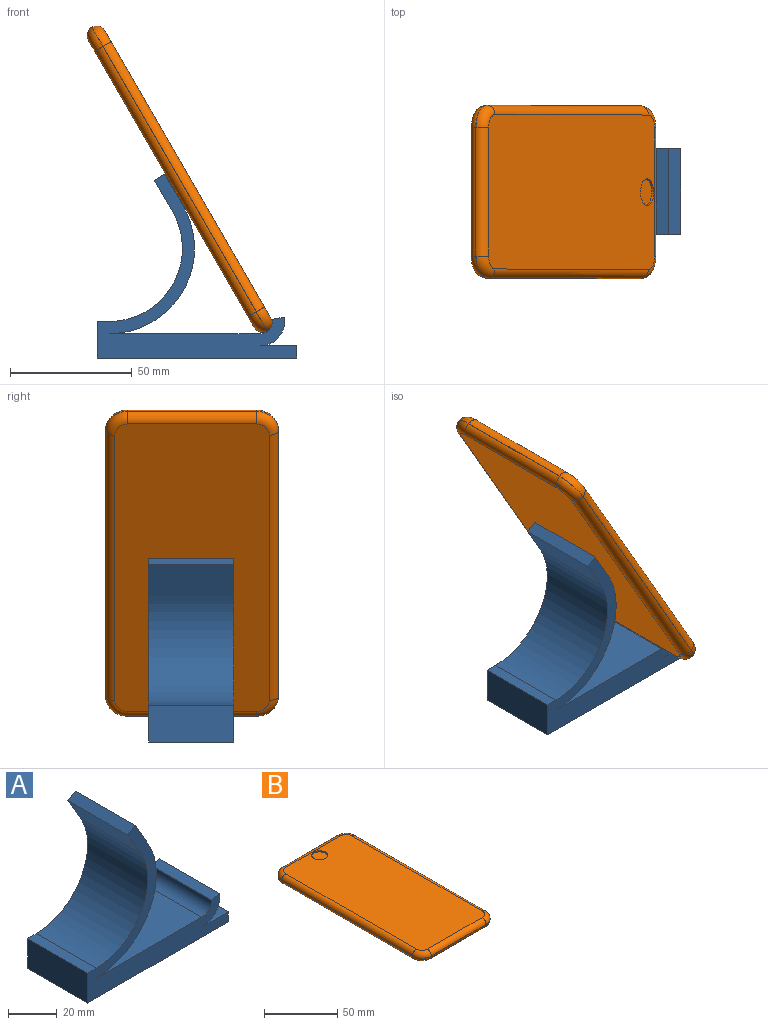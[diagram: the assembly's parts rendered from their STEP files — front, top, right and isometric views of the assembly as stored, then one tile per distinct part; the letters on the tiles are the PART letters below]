
ASSEMBLY  parts=2 mates=1
PART A: 23 faces, bbox 82x35x75.5 mm
  f0: plane 82x35mm, normal (0,0,-1), area 666mm2, adj f1,f2,f4,f16,f17,f18,f21,f22
  f1: plane 76x8mm, normal (0,1,0), area 528mm2, adj f0,f3,f18,f19,f20,f22
  f2: plane 76x8mm, normal (0,-1,0), area 528mm2, adj f0,f3,f18,f19,f20,f22
  f3: plane 60x29mm, normal (0,0,-1), area 1740mm2, adj f1,f2,f20,f22
  f4: plane 35x5mm, normal (1,0,0), area 175mm2, adj f0,f5,f16,f17
  f5: plane 35x15mm, normal (0,0,1), area 525mm2, adj f4,f6,f16,f17
  f6: cylinder r=10mm len=35mm, axis (0,1,0), area 611mm2, adj f5,f7,f16,f17
  f7: plane 35x4.92mm, normal (-0.17,0,0.98), area 175mm2, adj f6,f8,f16,f17
  f8: cylinder r=5mm len=35mm, axis (0,1,0), area 322.9mm2, adj f7,f9,f16,f17
  f9: plane 61.5x35mm, normal (0,0,1), area 2152.6mm2, adj f8,f10,f16,f17
  f10: cylinder r=35mm len=52.5mm, axis (0,1,0), area 2565.6mm2, adj f9,f11,f16,f17
  f11: plane 35x12.99mm, normal (0.87,0,0.5), area 525mm2, adj f10,f12,f16,f17
  f12: plane 35x4.33mm, normal (-0.5,0,0.87), area 175mm2, adj f11,f13,f16,f17
  f13: plane 35x12.99mm, normal (-0.87,0,-0.5), area 525mm2, adj f12,f14,f16,f17
  f14: cylinder r=30mm len=45mm, axis (0,1,0), area 2199.1mm2, adj f13,f15,f16,f17
  f15: plane 35x5mm, normal (0,0,1), area 175mm2, adj f14,f16,f17,f21
  f16: plane 82x75.49mm, normal (0,-1,0), area 1251.6mm2, adj f0,f4,f5,f6,f7,f8,f9,f10
  f17: plane 82x75.49mm, normal (0,1,0), area 1251.6mm2, adj f0,f4,f5,f6,f7,f8,f9,f10
  f18: plane 29x3mm, normal (-1,0,0), area 87mm2, adj f0,f1,f2,f19
  f19: plane 29x16mm, normal (0,0,-1), area 464mm2, adj f1,f2,f18,f20
  f20: plane 29x5mm, normal (-1,0,0), area 145mm2, adj f1,f2,f3,f19
  f21: plane 35x15mm, normal (-1,0,0), area 525mm2, adj f0,f15,f16,f17
  f22: plane 29x8mm, normal (1,0,0), area 232mm2, adj f0,f1,f2,f3
PART B: 28 faces, bbox 72.5x145.5x7.7 mm
  f0: plane 125.8x0.09mm, normal (1,0,0), area 11.3mm2, adj f7,f9,f11,f20
  f1: plane 136.4x63.4mm, normal (0,0,1), area 8530.3mm2, adj f10,f11,f12,f13,f14,f15,f16,f17
  f2: plane 125.8x0.09mm, normal (-1,0,0), area 11.3mm2, adj f6,f8,f16,f23
  f3: plane 136.4x63.4mm, normal (0,0,-1), area 8623.6mm2, adj f18,f19,f20,f21,f22,f23,f24,f25
  f4: plane 52.8x0.09mm, normal (0,-1,0), area 4.8mm2, adj f8,f9,f12,f19
  f5: plane 52.8x0.09mm, normal (0,1,0), area 4.8mm2, adj f6,f7,f15,f24
  f6: cylinder r=9.1mm len=9.1mm, axis (0,0,-1), area 1.3mm2, adj f2,f5,f17,f25
  f7: cylinder r=9.1mm len=9.1mm, axis (0,0,1), area 1.3mm2, adj f0,f5,f13,f22
  f8: cylinder r=9.1mm len=9.1mm, axis (0,0,1), area 1.3mm2, adj f2,f4,f14,f21
  f9: cylinder r=9.1mm len=9.1mm, axis (0,0,-1), area 1.3mm2, adj f0,f4,f10,f18
  f10: torus R=5.3mm, axis (0,0,-1), area 72.4mm2, adj f1,f9,f11,f12
  f11: cylinder r=3.8mm len=125.8mm, axis (0,-1,0), area 750.9mm2, adj f0,f1,f10,f13
  f12: cylinder r=3.8mm len=52.8mm, axis (1,0,0), area 315.2mm2, adj f1,f4,f10,f14
  f13: torus R=5.3mm, axis (0,0,-1), area 72.4mm2, adj f1,f7,f11,f15
  f14: torus R=5.3mm, axis (0,0,-1), area 72.4mm2, adj f1,f8,f12,f16
  f15: cylinder r=3.8mm len=52.8mm, axis (-1,0,0), area 315.2mm2, adj f1,f5,f13,f17
  f16: cylinder r=3.8mm len=125.8mm, axis (0,1,0), area 750.9mm2, adj f1,f2,f14,f17
  f17: torus R=5.3mm, axis (0,0,-1), area 72.4mm2, adj f1,f6,f15,f16
  f18: torus R=5.3mm, axis (0,0,-1), area 72.4mm2, adj f3,f9,f19,f20
  f19: cylinder r=3.8mm len=52.8mm, axis (-1,0,0), area 315.2mm2, adj f3,f4,f18,f21
  f20: cylinder r=3.8mm len=125.8mm, axis (0,1,0), area 750.9mm2, adj f0,f3,f18,f22
  f21: torus R=5.3mm, axis (0,0,-1), area 72.4mm2, adj f3,f8,f19,f23
  f22: torus R=5.3mm, axis (0,0,-1), area 72.4mm2, adj f3,f7,f20,f24
  f23: cylinder r=3.8mm len=125.8mm, axis (0,-1,0), area 750.9mm2, adj f2,f3,f21,f25
  f24: cylinder r=3.8mm len=52.8mm, axis (1,0,0), area 315.2mm2, adj f3,f5,f22,f25
  f25: torus R=5.3mm, axis (0,0,-1), area 72.4mm2, adj f3,f6,f23,f24
  f26: cylinder r=5.45mm len=10.9mm, axis (0,0,1), area 34.2mm2, adj f1,f27
  f27: plane 10.9x10.9mm, normal (0,0,1), area 93.3mm2, adj f26
PLACE A t=(-40.08,22.36,-9.59)mm
PLACE B rot(axis=(-0.45,0.45,-0.77),104.5deg) t=(-12.24,4.54,-3.5)mm
MATE parallel B.f3 <-> A.f11  axis (-0.87,0,-0.5) through (-85.67,4.54,115.99)mm
